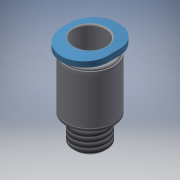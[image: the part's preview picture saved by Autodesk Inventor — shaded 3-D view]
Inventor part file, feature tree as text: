
AUTODESK INVENTOR PART (.ipt)
format: ipt  version: 2017.1 (Build 211199000, 199)  size: 212,480 bytes
history: native  units: mm
features: other x21, sketch x4, revolve x2, extrude x2, thread x1
ambient origin geometry x8: Origin, YZ Plane, XZ Plane, XY Plane, X Axis, Y Axis, Z Axis, Center Point
bodies: Solid1 (feature_tree)
feature tree (30):
  revolve  "Revolution1"  [1 undecoded]
  thread  "Thread1"  [1 undecoded]
  extrude  "Extrusion1"  TaperAngle=360.0deg  [1 undecoded]
  extrude  "Extrusion2"  [1 undecoded]
  revolve  "Revolution2"  [1 undecoded]
  other  "ANBAU_XY"
  other  "ANBAU_YZ"
  other  "ANBAU_ZX"
  other  "ANBAU_X"
  other  "ANBAU_Y"
  other  "ANBAU_Z"
  other  "ANBAU_Center"
  other  "CPV_XY"
  other  "CPV_YZ"
  other  "CPV_ZX"
  other  "CPV_X"
  other  "CPV_Y"
  other  "CPV_Z"
  other  "CPV_Center"
  other  "CPV_ANBAU_XY"
  other  "CPV_ANBAU_YZ"
  other  "CPV_ANBAU_ZX"
  other  "CPV_ANBAU_X"
  other  "CPV_ANBAU_Y"
  other  "CPV_ANBAU_Z"
  other  "CPV_ANBAU_Center"
  sketch  "Sketch_1"  dims[d0=360.0deg d1=4.3865mm d2=0.0mm d3=1.5mm d4=0.0mm]
  sketch  "Sketch_2"  dims[d5=7.2mm d6=0.0mm d7=360.0deg]
  sketch  "Sketch_3"
  sketch  "Sketch_4"
note: 5 required parameter values undecoded (feature->parameter linkage not recoverable at this tier; creation-order binding heuristic only, values carry confidence <= 0.55)